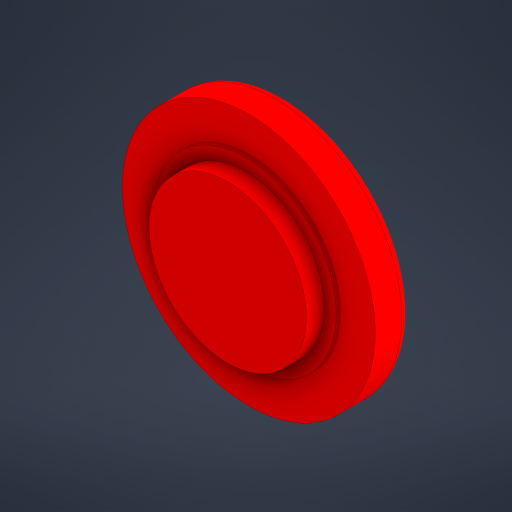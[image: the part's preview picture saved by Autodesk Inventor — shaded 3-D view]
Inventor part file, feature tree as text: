
AUTODESK INVENTOR PART (.ipt)
format: ipt  version: 2023.4 (Build 274418000, 418)  size: 310,784 bytes
history: native  units: mm
features: extrude x4, sketch x2, fillet x1, chamfer x1
ambient origin geometry x8: Origin, YZ Plane, XZ Plane, XY Plane, X Axis, Y Axis, Z Axis, Center Point
bodies: Solid1 (feature_tree)
feature tree (8):
  sketch  "Sketch1"  dims[d0=22.25mm d1=25.75mm]
  extrude  "Extrusion1"  Depth=25.75mm
  extrude  "Extrusion2"  Depth=5.0mm TaperAngle=0.0deg
  extrude  "Extrusion3"  Depth=0.5mm TaperAngle=0.0deg
  fillet  "Fillet1"  Radius=2.5mm
  extrude  "Extrusion4"  Depth=1.25mm
  chamfer  "Chamfer1"  Distance=25.0mm
  sketch  "Sketch2"  dims[d2=5.0mm d3=5.0mm d4=0.0mm d5=0.5mm d6=0.0mm d7=2.5mm d8=0.0mm d9=1.25mm d10=25.0mm d11=25.0mm d12=0.25mm d13=0.0mm d14=0.25mm d15=2.0mm d16=45.0deg]
